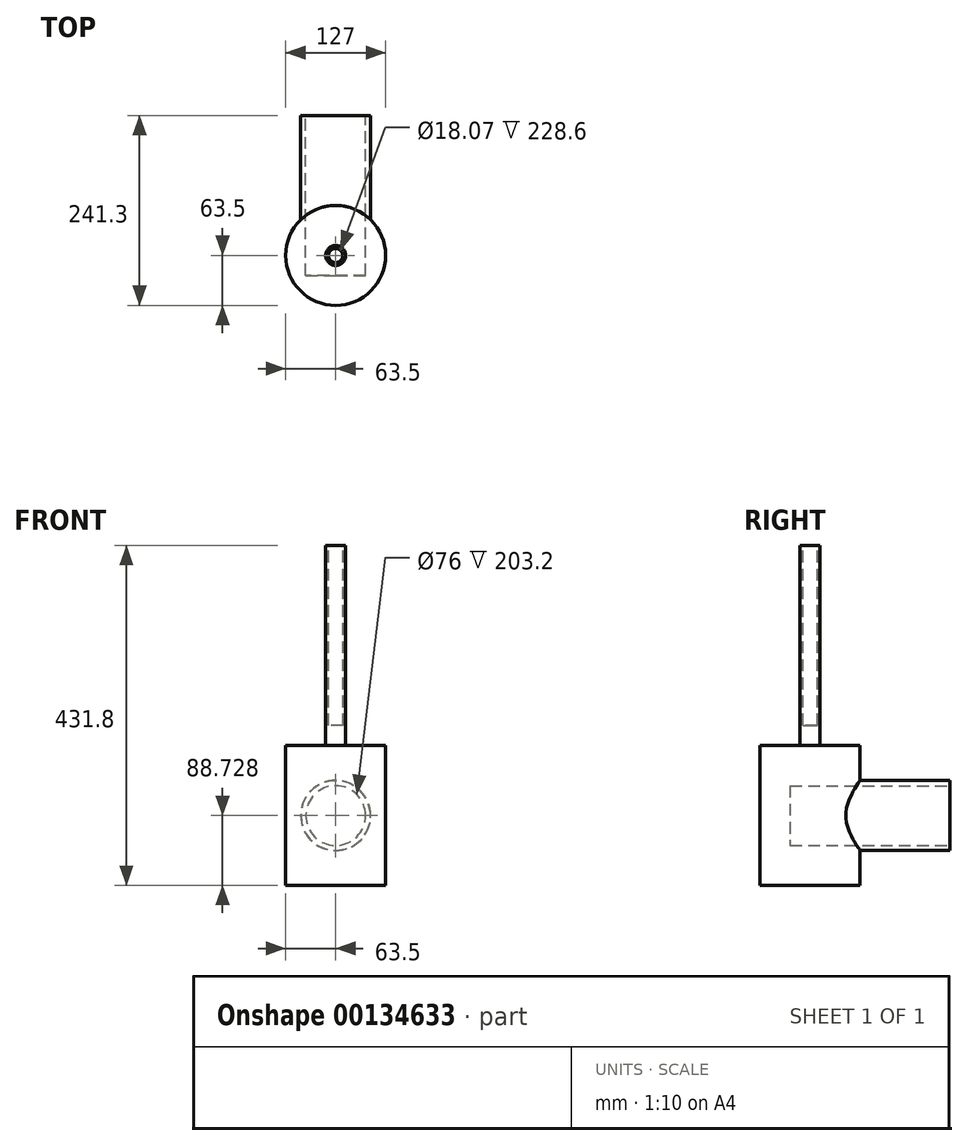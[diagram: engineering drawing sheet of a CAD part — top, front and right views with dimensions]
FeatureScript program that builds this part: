
annotation { "Feature Type Name" : "Feature", "Feature Type Description" : "" }
export const myFeature = defineFeature(function(context is Context, id is Id, definition is map)
    precondition{}
    {
        {
            var Q0;
            Q0=qCreatedBy(makeId("Top.planeOp"),FACE);
            var sketch = newSketch(context, id + "F0", { "sketchPlane" : qUnion([Q0])});
            skCircle(sketch, "E0", {"center": v(0, 0) * mm, "radius": 63.5 * mm});
            skSolve(sketch);
        }
        {
            var Q0;
            Q0 = qSketchRegion(id + "F0", true);
            extrude(context, id + "F1", {"entities" : qUnion([Q0]), "depth" : 177.8 * mm});
        }
        {
            var Q0;
            Q0=qCreatedBy(makeId("Front.planeOp"),FACE);
            var sketch = newSketch(context, id + "F2", { "sketchPlane" : qUnion([Q0])});
            skLineSegment(sketch, "E1", {"start": v(0, 0) * mm, "end": v(0, 88.9) * mm});
            skCircle(sketch, "E2", {"center": v(0, 88.9) * mm, "radius": 44.45 * mm});
            skSolve(sketch);
        }
        {
            var Q0;
            Q0 = qSketchRegion(id + "F2", true);
            extrude(context, id + "F3", {"entities" : qUnion([Q0]), "operationType" : NewBodyOperationType.ADD, "oppositeDirection" : true, "depth" : 177.8 * mm});
        }
        {
            var Q0;
            Q0=makeQuery(id+"F3.opExtrude","CAP_FACE",FACE,{"disambiguationData":[OSD([sQuery(id+"F2.wireOp",EDGE,"E2")])],"isStart":false});
            var sketch = newSketch(context, id + "F4", { "sketchPlane" : qUnion([Q0])});
            skCircle(sketch, "E3", {"center": v(0, 88.9) * mm, "radius": 44.45 * mm});
            skSolve(sketch);
        }
        {
            var Q0;
            Q0=makeQuery(id+"F1.opExtrude","CAP_FACE",FACE,{"disambiguationData":[OSD([sQuery(id+"F0.wireOp",EDGE,"E0")])],"isStart":false});
            var sketch = newSketch(context, id + "F5", { "sketchPlane" : qUnion([Q0])});
            skCircle(sketch, "E4", {"center": v(0, 0) * mm, "radius": 12.7 * mm});
            skSolve(sketch);
        }
        {
            var Q0;
            Q0=makeQuery(id+"F5.imprint","IMPRINT",FACE,{"disambiguationData":[TD([[makeQuery(id+"F5.imprint","IMPRINT",EDGE,{"derivedFrom":sQuery(id+"F5.wireOp",EDGE,"E4")}),1.0]])]});
            extrude(context, id + "F6", {"entities" : qUnion([Q0]), "operationType" : NewBodyOperationType.ADD, "depth" : 254 * mm});
        }
        {
            var Q0;
            Q0=makeQuery(id+"F4.imprint","IMPRINT",FACE,{"disambiguationData":[TD([[makeQuery(id+"F4.imprint","IMPRINT",EDGE,{"derivedFrom":sQuery(id+"F4.wireOp",EDGE,"E3")}),-1.0]])]});
            var sketch = newSketch(context, id + "F7", { "sketchPlane" : qUnion([Q0])});
            skCircle(sketch, "E5", {"center": v(0, 88.73) * mm, "radius": 38 * mm});
            skSolve(sketch);
        }
        {
            var Q0;
            Q0 = qSketchRegion(id + "F7", true);
            extrude(context, id + "F8", {"entities" : qUnion([Q0]), "operationType" : NewBodyOperationType.REMOVE, "oppositeDirection" : true, "depth" : 203.2 * mm});
        }
        {
            var Q0;
            Q0=makeQuery(id+"F6.opExtrude","CAP_FACE",FACE,{"disambiguationData":[OSD([sQuery(id+"F5.wireOp",EDGE,"E4")])],"isStart":false});
            var sketch = newSketch(context, id + "F9", { "sketchPlane" : qUnion([Q0])});
            skCircle(sketch, "E6", {"center": v(0, 0) * mm, "radius": 9.04 * mm});
            skSolve(sketch);
        }
        {
            var Q0;
            Q0 = qSketchRegion(id + "F9", true);
            extrude(context, id + "F10", {"entities" : qUnion([Q0]), "operationType" : NewBodyOperationType.REMOVE, "oppositeDirection" : true, "depth" : 228.6 * mm});
        }
    });
